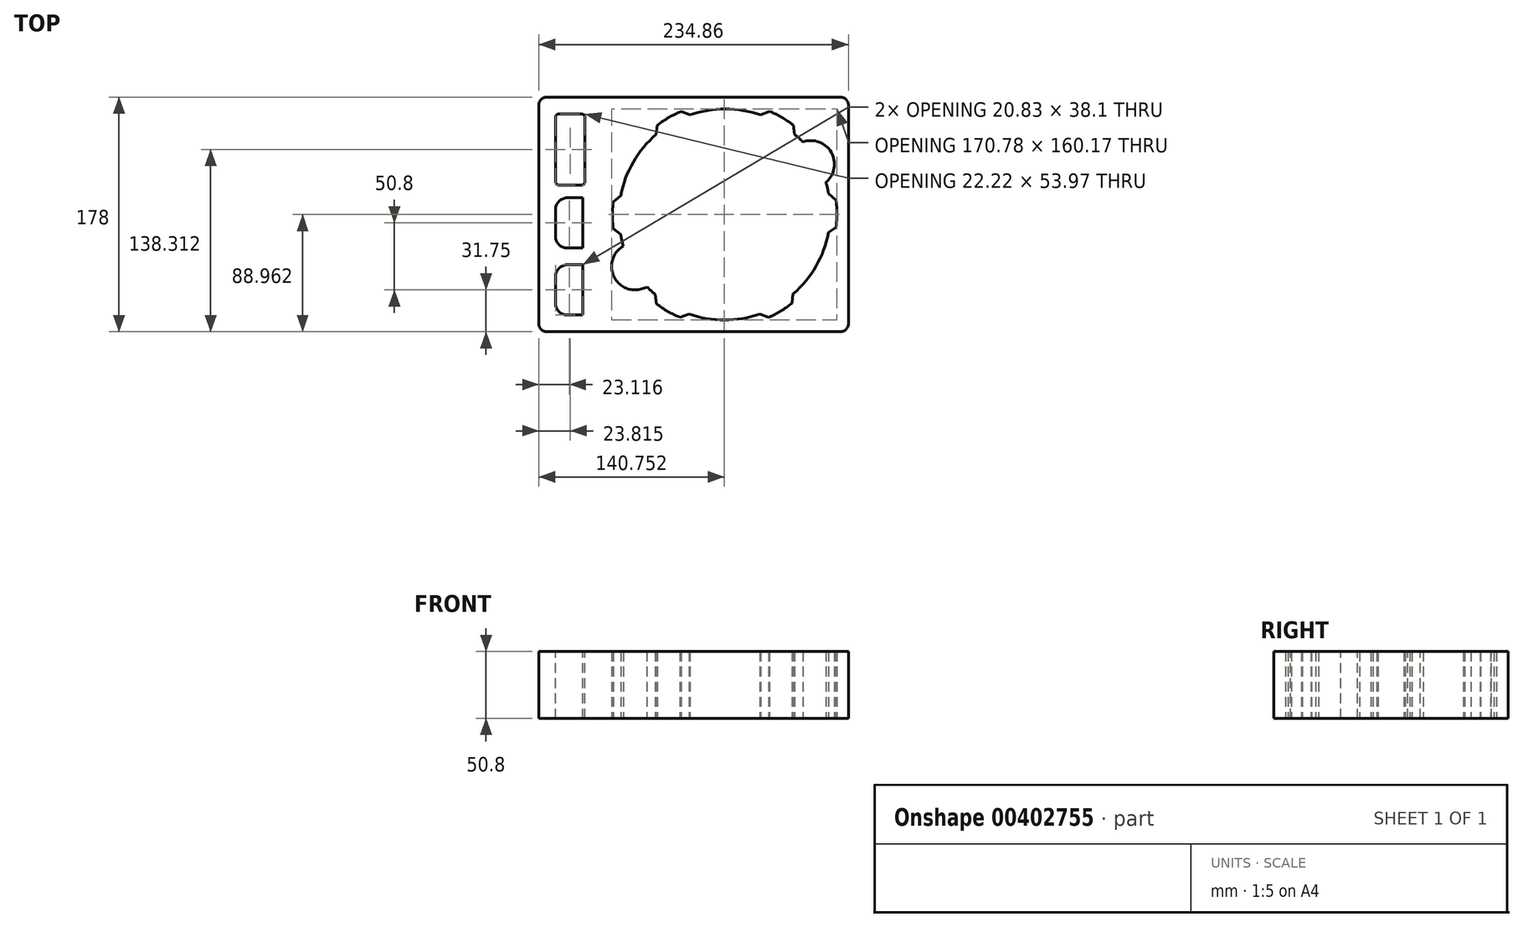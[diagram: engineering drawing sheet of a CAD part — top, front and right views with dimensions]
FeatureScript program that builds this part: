
annotation { "Feature Type Name" : "Feature", "Feature Type Description" : "" }
export const myFeature = defineFeature(function(context is Context, id is Id, definition is map)
    precondition{}
    {
        {
            var Q0;
            Q0=qCreatedBy(makeId("Top.planeOp"),FACE);
            var sketch = newSketch(context, id + "F0", { "sketchPlane" : qUnion([Q0])});
            skLineSegment(sketch, "E0", {"start": v(-117.43, 89) * mm, "end": v(117.43, -89) * mm, "construction": true});
            skLineSegment(sketch, "E1", {"start": v(117.43, 89) * mm, "end": v(0, 0) * mm, "construction": true});
            skArc(sketch, "E2", {"start": v(-70.48, 61.75) * mm, "mid": v(-79.05, 58.35) * mm, "end": v(-83.6, 50.33) * mm, "construction": true});
            skArc(sketch, "E3", {"start": v(-79.19, 70.45) * mm, "mid": v(-88.89, 80.1) * mm, "end": v(-98.64, 70.5) * mm, "construction": true});
            skArc(sketch, "E4", {"start": v(-98.68, -70.37) * mm, "mid": v(-88.97, -80.06) * mm, "end": v(-79.13, -70.5) * mm, "construction": true});
            skArc(sketch, "E5", {"start": v(-60.91, 9.68) * mm, "mid": v(-61.6, -0.56) * mm, "end": v(-60.92, -10.8) * mm});
            skLineSegment(sketch, "E6", {"start": v(-79.19, 70.45) * mm, "end": v(-70.48, 70.45) * mm, "construction": true});
            skLineSegment(sketch, "E7", {"start": v(-70.48, 70.45) * mm, "end": v(-70.48, 61.75) * mm, "construction": true});
            skLineSegment(sketch, "E8", {"start": v(-83.6, 50.33) * mm, "end": v(-83.6, 22.87) * mm, "construction": true});
            skLineSegment(sketch, "E9", {"start": v(-83.6, 22.87) * mm, "end": v(-77.26, 22.87) * mm, "construction": true});
            skLineSegment(sketch, "E10", {"start": v(-77.26, 22.87) * mm, "end": v(-77.26, -10.83) * mm, "construction": true});
            skLineSegment(sketch, "E11", {"start": v(-77.26, -10.83) * mm, "end": v(-70.83, -10.83) * mm, "construction": true});
            skLineSegment(sketch, "E12", {"start": v(-70.83, -10.83) * mm, "end": v(-70.83, -70.5) * mm, "construction": true});
            skLineSegment(sketch, "E13", {"start": v(-70.83, -70.5) * mm, "end": v(-79.13, -70.5) * mm, "construction": true});
            skLineSegment(sketch, "E14", {"start": v(-98.68, -70.37) * mm, "end": v(-105.43, -65.75) * mm, "construction": true});
            skLineSegment(sketch, "E15", {"start": v(-108.04, -64.7) * mm, "end": v(-108.04, -60.76) * mm, "construction": true});
            skLineSegment(sketch, "E16", {"start": v(-108.04, -60.76) * mm, "end": v(-106.9, -60.74) * mm, "construction": true});
            skLineSegment(sketch, "E17", {"start": v(-106.9, -60.74) * mm, "end": v(-106.9, 53.14) * mm, "construction": true});
            skLineSegment(sketch, "E18", {"start": v(-106.9, 53.14) * mm, "end": v(-108.07, 53.14) * mm, "construction": true});
            skLineSegment(sketch, "E19", {"start": v(-108.07, 53.14) * mm, "end": v(-108.07, 57.12) * mm, "construction": true});
            skLineSegment(sketch, "E20", {"start": v(-108.07, 57.12) * mm, "end": v(-106.9, 57.12) * mm, "construction": true});
            skLineSegment(sketch, "E21", {"start": v(-106.9, 57.12) * mm, "end": v(-107.04, 63.36) * mm, "construction": true});
            skLineSegment(sketch, "E22", {"start": v(-107.04, 63.36) * mm, "end": v(-98.64, 70.5) * mm, "construction": true});
            skArc(sketch, "E23", {"start": v(-9.49, 78.12) * mm, "mid": v(-18.8, 73.53) * mm, "end": v(-27.4, 67.74) * mm});
            skArc(sketch, "E24", {"start": v(75.52, 67.88) * mm, "mid": v(66.9, 73.6) * mm, "end": v(57.61, 78.19) * mm});
            skArc(sketch, "E25", {"start": v(108.1, -9.7) * mm, "mid": v(108.7, 0.59) * mm, "end": v(108.05, 10.87) * mm});
            skArc(sketch, "E26", {"start": v(56.9, -78.11) * mm, "mid": v(66.08, -73.32) * mm, "end": v(74.54, -67.34) * mm});
            skArc(sketch, "E27", {"start": v(-28.12, -67.82) * mm, "mid": v(-19.56, -73.56) * mm, "end": v(-10.29, -78.05) * mm});
            skArc(sketch, "E28", {"start": v(-28.4, 60.74) * mm, "mid": v(-45.75, 39.78) * mm, "end": v(-55.21, 14.26) * mm});
            skArc(sketch, "E29", {"start": v(50.94, 75.43) * mm, "mid": v(24.1, 80.05) * mm, "end": v(-2.74, 75.43) * mm});
            skArc(sketch, "E30", {"start": v(82.84, 54.94) * mm, "mid": v(79.78, 57.95) * mm, "end": v(76.52, 60.75) * mm});
            skArc(sketch, "E31", {"start": v(102.32, 15.8) * mm, "mid": v(101.51, 20.16) * mm, "end": v(100.4, 24.44) * mm});
            skArc(sketch, "E32", {"start": v(75.47, -60.27) * mm, "mid": v(92.86, -39.3) * mm, "end": v(102.35, -13.78) * mm});
            skArc(sketch, "E33", {"start": v(-3.58, -75.5) * mm, "mid": v(23.34, -80.12) * mm, "end": v(50.25, -75.43) * mm});
            skArc(sketch, "E34", {"start": v(-35.4, -54.87) * mm, "mid": v(-32.33, -57.87) * mm, "end": v(-29.07, -60.67) * mm});
            skArc(sketch, "E35", {"start": v(-55.22, -15.34) * mm, "mid": v(-54.43, -19.69) * mm, "end": v(-53.33, -23.97) * mm});
            skLineSegment(sketch, "E36", {"start": v(-55.22, -15.34) * mm, "end": v(-60.92, -10.8) * mm});
            skLineSegment(sketch, "E37", {"start": v(-60.91, 9.68) * mm, "end": v(-55.21, 14.26) * mm});
            skLineSegment(sketch, "E38", {"start": v(-28.4, 60.74) * mm, "end": v(-27.4, 67.74) * mm});
            skLineSegment(sketch, "E39", {"start": v(-9.49, 78.12) * mm, "end": v(-2.74, 75.43) * mm});
            skLineSegment(sketch, "E40", {"start": v(50.94, 75.43) * mm, "end": v(57.61, 78.19) * mm});
            skLineSegment(sketch, "E41", {"start": v(75.52, 67.88) * mm, "end": v(76.52, 60.75) * mm});
            skLineSegment(sketch, "E42", {"start": v(102.32, 15.8) * mm, "end": v(108.05, 10.87) * mm});
            skLineSegment(sketch, "E43", {"start": v(108.1, -9.7) * mm, "end": v(102.35, -13.78) * mm});
            skLineSegment(sketch, "E44", {"start": v(75.47, -60.27) * mm, "end": v(74.54, -67.34) * mm});
            skLineSegment(sketch, "E45", {"start": v(56.9, -78.11) * mm, "end": v(50.25, -75.43) * mm});
            skLineSegment(sketch, "E46", {"start": v(-10.29, -78.05) * mm, "end": v(-3.58, -75.5) * mm});
            skLineSegment(sketch, "E47", {"start": v(-28.12, -67.82) * mm, "end": v(-29.07, -60.67) * mm});
            skLineSegment(sketch, "E48", {"start": v(-117.43, 82.9) * mm, "end": v(-117.43, -82.9) * mm});
            skLineSegment(sketch, "E49", {"start": v(-111.33, -89) * mm, "end": v(111.33, -89) * mm});
            skLineSegment(sketch, "E50", {"start": v(117.43, -82.9) * mm, "end": v(117.43, 82.9) * mm});
            skLineSegment(sketch, "E51", {"start": v(111.33, 89) * mm, "end": v(-111.33, 89) * mm});
            skPoint(sketch, "E52.visualSharp", {"position": v(-117.43, 89) * mm});
            skArc(sketch, "E52.filletArc", {"start": v(-111.33, 89) * mm, "mid": v(-115.64, 87.21) * mm, "end": v(-117.43, 82.9) * mm});
            skPoint(sketch, "E53.visualSharp", {"position": v(117.43, 89) * mm});
            skArc(sketch, "E53.filletArc", {"start": v(117.43, 82.9) * mm, "mid": v(115.64, 87.21) * mm, "end": v(111.33, 89) * mm});
            skPoint(sketch, "E54.visualSharp", {"position": v(117.43, -89) * mm});
            skArc(sketch, "E54.filletArc", {"start": v(111.33, -89) * mm, "mid": v(115.64, -87.21) * mm, "end": v(117.43, -82.9) * mm});
            skPoint(sketch, "E55.visualSharp", {"position": v(-117.43, -89) * mm});
            skArc(sketch, "E55.filletArc", {"start": v(-117.43, -82.9) * mm, "mid": v(-115.64, -87.21) * mm, "end": v(-111.33, -89) * mm});
            skLineSegment(sketch, "E56", {"start": v(-108.04, -60.76) * mm, "end": v(-108.07, 53.14) * mm, "construction": true});
            skLineSegment(sketch, "E57", {"start": v(-107.04, 63.36) * mm, "end": v(-108.07, 57.12) * mm, "construction": true});
            skArc(sketch, "E58", {"start": v(-105.43, -65.75) * mm, "mid": v(-106.7, -65.12) * mm, "end": v(-108.04, -64.7) * mm, "construction": true});
            skArc(sketch, "E59", {"start": v(100.4, 24.44) * mm, "mid": v(104.45, 47.07) * mm, "end": v(82.84, 54.94) * mm});
            skArc(sketch, "E60", {"start": v(-53.33, -23.97) * mm, "mid": v(-59.81, -48.38) * mm, "end": v(-35.4, -54.87) * mm});
            skPoint(sketch, "E60.midSnap0", {"position": v(-35.4, -54.87) * mm});
            skPoint(sketch, "E60.midSnap1", {"position": v(-53.33, -23.97) * mm});
            skSolve(sketch);
        }
        {
            var Q0;
            Q0=qSketchRegion(id+"F0",true);
            extrude(context, id + "F1", {"entities" : qUnion([Q0]), "depth" : 50.8 * mm, "offsetDistance" : 25.4 * mm});
        }
        {
            var Q0;
            Q0=makeQuery(id+"F1.opExtrude","CAP_FACE",FACE,{"disambiguationData":[OSD([sQuery(id+"F0.wireOp",EDGE,"E5"),sQuery(id+"F0.wireOp",EDGE,"E23"),sQuery(id+"F0.wireOp",EDGE,"E24"),sQuery(id+"F0.wireOp",EDGE,"E25"),sQuery(id+"F0.wireOp",EDGE,"E26"),sQuery(id+"F0.wireOp",EDGE,"E27"),sQuery(id+"F0.wireOp",EDGE,"E28"),sQuery(id+"F0.wireOp",EDGE,"E29"),sQuery(id+"F0.wireOp",EDGE,"E30"),sQuery(id+"F0.wireOp",EDGE,"E31"),sQuery(id+"F0.wireOp",EDGE,"E32"),sQuery(id+"F0.wireOp",EDGE,"E33"),sQuery(id+"F0.wireOp",EDGE,"E34"),sQuery(id+"F0.wireOp",EDGE,"E35"),sQuery(id+"F0.wireOp",EDGE,"E36"),sQuery(id+"F0.wireOp",EDGE,"E37"),sQuery(id+"F0.wireOp",EDGE,"E38"),sQuery(id+"F0.wireOp",EDGE,"E39"),sQuery(id+"F0.wireOp",EDGE,"E40"),sQuery(id+"F0.wireOp",EDGE,"E41"),sQuery(id+"F0.wireOp",EDGE,"E42"),sQuery(id+"F0.wireOp",EDGE,"E43"),sQuery(id+"F0.wireOp",EDGE,"E44"),sQuery(id+"F0.wireOp",EDGE,"E45"),sQuery(id+"F0.wireOp",EDGE,"E46"),sQuery(id+"F0.wireOp",EDGE,"E47"),sQuery(id+"F0.wireOp",EDGE,"E48"),sQuery(id+"F0.wireOp",EDGE,"E49"),sQuery(id+"F0.wireOp",EDGE,"E50"),sQuery(id+"F0.wireOp",EDGE,"E51"),sQuery(id+"F0.wireOp",EDGE,"E52.filletArc"),sQuery(id+"F0.wireOp",EDGE,"E53.filletArc"),sQuery(id+"F0.wireOp",EDGE,"E54.filletArc"),sQuery(id+"F0.wireOp",EDGE,"E55.filletArc"),sQuery(id+"F0.wireOp",EDGE,"E59"),sQuery(id+"F0.wireOp",EDGE,"E60")])],"isStart":false});
            var sketch = newSketch(context, id + "F2", { "sketchPlane" : qUnion([Q0])});
            skLineSegment(sketch, "E61.bottom", {"start": v(-104.73, -76.3) * mm, "end": v(-104.73, -38.2) * mm});
            skLineSegment(sketch, "E61.top", {"start": v(-83.9, -76.3) * mm, "end": v(-83.9, -38.2) * mm});
            skLineSegment(sketch, "E61.left", {"start": v(-104.73, -76.3) * mm, "end": v(-83.9, -76.3) * mm});
            skLineSegment(sketch, "E61.right", {"start": v(-104.73, -38.2) * mm, "end": v(-83.9, -38.2) * mm});
            skLineSegment(sketch, "E62", {"start": v(-62.2, -40.25) * mm, "end": v(-62.2, 42.66) * mm, "construction": true});
            skLineSegment(sketch, "E63", {"start": v(-62.2, 42.66) * mm, "end": v(-62.2, 89) * mm, "construction": true});
            skLineSegment(sketch, "E64", {"start": v(-62.2, -40.25) * mm, "end": v(-62.2, -89) * mm, "construction": true});
            skLineSegment(sketch, "E65", {"start": v(-62.2, -89) * mm, "end": v(-68.55, -89) * mm, "construction": true});
            skLineSegment(sketch, "E66", {"start": v(-68.55, -89) * mm, "end": v(-68.55, 89) * mm, "construction": true});
            skLineSegment(sketch, "E67", {"start": v(-70.82, -89) * mm, "end": v(-70.82, 89) * mm, "construction": true});
            skLineSegment(sketch, "E68.0.1.0", {"start": v(-104.73, -25.5) * mm, "end": v(-83.9, -25.5) * mm});
            skLineSegment(sketch, "E68.0.1.1", {"start": v(-104.73, -25.5) * mm, "end": v(-104.73, 12.6) * mm});
            skLineSegment(sketch, "E68.0.1.2", {"start": v(-83.9, -25.5) * mm, "end": v(-83.9, 12.6) * mm});
            skLineSegment(sketch, "E68.0.1.3", {"start": v(-104.73, 12.6) * mm, "end": v(-83.9, 12.6) * mm});
            skLineSegment(sketch, "E68.direction1", {"start": v(-104.73, -76.3) * mm, "end": v(-78.31, -76.3) * mm, "construction": true});
            skLineSegment(sketch, "E68.direction2", {"start": v(-104.73, -76.3) * mm, "end": v(-104.73, -25.5) * mm, "construction": true});
            skSolve(sketch);
        }
        {
            var Q0;
            Q0=qSketchRegion(id+"F2",true);
            extrude(context, id + "F3", {"entities" : qUnion([Q0]), "operationType" : NewBodyOperationType.REMOVE, "oppositeDirection" : true, "depth" : 50.8 * mm, "offsetDistance" : 25.4 * mm});
        }
        {
            var Q0;
            Q0=makeQuery(id+"F1.opExtrude","CAP_FACE",FACE,{"disambiguationData":[OSD([sQuery(id+"F0.wireOp",EDGE,"E5"),sQuery(id+"F0.wireOp",EDGE,"E23"),sQuery(id+"F0.wireOp",EDGE,"E24"),sQuery(id+"F0.wireOp",EDGE,"E25"),sQuery(id+"F0.wireOp",EDGE,"E26"),sQuery(id+"F0.wireOp",EDGE,"E27"),sQuery(id+"F0.wireOp",EDGE,"E28"),sQuery(id+"F0.wireOp",EDGE,"E29"),sQuery(id+"F0.wireOp",EDGE,"E30"),sQuery(id+"F0.wireOp",EDGE,"E31"),sQuery(id+"F0.wireOp",EDGE,"E32"),sQuery(id+"F0.wireOp",EDGE,"E33"),sQuery(id+"F0.wireOp",EDGE,"E34"),sQuery(id+"F0.wireOp",EDGE,"E35"),sQuery(id+"F0.wireOp",EDGE,"E36"),sQuery(id+"F0.wireOp",EDGE,"E37"),sQuery(id+"F0.wireOp",EDGE,"E38"),sQuery(id+"F0.wireOp",EDGE,"E39"),sQuery(id+"F0.wireOp",EDGE,"E40"),sQuery(id+"F0.wireOp",EDGE,"E41"),sQuery(id+"F0.wireOp",EDGE,"E42"),sQuery(id+"F0.wireOp",EDGE,"E43"),sQuery(id+"F0.wireOp",EDGE,"E44"),sQuery(id+"F0.wireOp",EDGE,"E45"),sQuery(id+"F0.wireOp",EDGE,"E46"),sQuery(id+"F0.wireOp",EDGE,"E47"),sQuery(id+"F0.wireOp",EDGE,"E48"),sQuery(id+"F0.wireOp",EDGE,"E49"),sQuery(id+"F0.wireOp",EDGE,"E50"),sQuery(id+"F0.wireOp",EDGE,"E51"),sQuery(id+"F0.wireOp",EDGE,"E52.filletArc"),sQuery(id+"F0.wireOp",EDGE,"E53.filletArc"),sQuery(id+"F0.wireOp",EDGE,"E54.filletArc"),sQuery(id+"F0.wireOp",EDGE,"E55.filletArc"),sQuery(id+"F0.wireOp",EDGE,"E59"),sQuery(id+"F0.wireOp",EDGE,"E60")])],"isStart":false});
            var sketch = newSketch(context, id + "F4", { "sketchPlane" : qUnion([Q0])});
            skLineSegment(sketch, "E69.bottom", {"start": v(-104.73, 76.3) * mm, "end": v(-104.73, 22.32) * mm});
            skLineSegment(sketch, "E69.top", {"start": v(-82.5, 76.3) * mm, "end": v(-82.5, 22.32) * mm});
            skLineSegment(sketch, "E69.left", {"start": v(-104.73, 76.3) * mm, "end": v(-82.5, 76.3) * mm});
            skLineSegment(sketch, "E69.right", {"start": v(-104.73, 22.32) * mm, "end": v(-82.5, 22.32) * mm});
            skSolve(sketch);
        }
        {
            var Q0;
            Q0=qSketchRegion(id+"F4",true);
            extrude(context, id + "F5", {"entities" : qUnion([Q0]), "operationType" : NewBodyOperationType.REMOVE, "oppositeDirection" : true, "depth" : 50.8 * mm, "offsetDistance" : 25.4 * mm});
        }
        {
            var Q0;
            Q0=makeQuery(id+"F3.boolean.opBoolean","COPY",EDGE,{"derivedFrom":makeQuery(id+"F3.opExtrude","SWEPT_EDGE",EDGE,{"disambiguationData":[OSD([sQuery(id+"F2.wireOp",EDGE,"E68.0.1.1"),sQuery(id+"F2.wireOp",EDGE,"E68.0.1.3")])]})});
            var Q1;
            Q1=makeQuery(id+"F3.boolean.opBoolean","COPY",EDGE,{"derivedFrom":makeQuery(id+"F3.opExtrude","SWEPT_EDGE",EDGE,{"disambiguationData":[OSD([sQuery(id+"F2.wireOp",EDGE,"E61.bottom"),sQuery(id+"F2.wireOp",EDGE,"E61.right")])]})});
            var Q2;
            Q2=makeQuery(id+"F3.boolean.opBoolean","COPY",EDGE,{"derivedFrom":makeQuery(id+"F3.opExtrude","SWEPT_EDGE",EDGE,{"disambiguationData":[OSD([sQuery(id+"F2.wireOp",EDGE,"E68.0.1.0"),sQuery(id+"F2.wireOp",EDGE,"E68.0.1.1")])]})});
            var Q3;
            Q3=makeQuery(id+"F3.boolean.opBoolean","COPY",EDGE,{"derivedFrom":makeQuery(id+"F3.opExtrude","SWEPT_EDGE",EDGE,{"disambiguationData":[OSD([sQuery(id+"F2.wireOp",EDGE,"E61.bottom"),sQuery(id+"F2.wireOp",EDGE,"E61.left")])]})});
            fillet(context, id + "F6", {"entities" : qUnion([Q0, Q1, Q2, Q3]), "tangentPropagation" : true, "radius" : 8.9 * mm, "defaultsChanged" : false, "vertexSettings" : [], "allowEdgeOverflow" : false});
        }
        {
            var Q0;
            Q0=makeQuery(id+"F5.boolean.opBoolean","COPY",EDGE,{"derivedFrom":makeQuery(id+"F5.opExtrude","SWEPT_EDGE",EDGE,{"disambiguationData":[OSD([sQuery(id+"F4.wireOp",EDGE,"E69.top"),sQuery(id+"F4.wireOp",EDGE,"E69.left")])]})});
            var Q1;
            Q1=makeQuery(id+"F5.boolean.opBoolean","COPY",EDGE,{"derivedFrom":makeQuery(id+"F5.opExtrude","SWEPT_EDGE",EDGE,{"disambiguationData":[OSD([sQuery(id+"F4.wireOp",EDGE,"E69.bottom"),sQuery(id+"F4.wireOp",EDGE,"E69.left")])]})});
            var Q2;
            Q2=makeQuery(id+"F5.boolean.opBoolean","COPY",EDGE,{"derivedFrom":makeQuery(id+"F5.opExtrude","SWEPT_EDGE",EDGE,{"disambiguationData":[OSD([sQuery(id+"F4.wireOp",EDGE,"E69.top"),sQuery(id+"F4.wireOp",EDGE,"E69.right")])]})});
            var Q3;
            Q3=makeQuery(id+"F5.boolean.opBoolean","COPY",EDGE,{"derivedFrom":makeQuery(id+"F5.opExtrude","SWEPT_EDGE",EDGE,{"disambiguationData":[OSD([sQuery(id+"F4.wireOp",EDGE,"E69.bottom"),sQuery(id+"F4.wireOp",EDGE,"E69.right")])]})});
            fillet(context, id + "F7", {"entities" : qUnion([Q0, Q1, Q2, Q3]), "tangentPropagation" : true, "radius" : 2.54 * mm, "defaultsChanged" : true, "vertexSettings" : [], "allowEdgeOverflow" : false});
        }
    });
